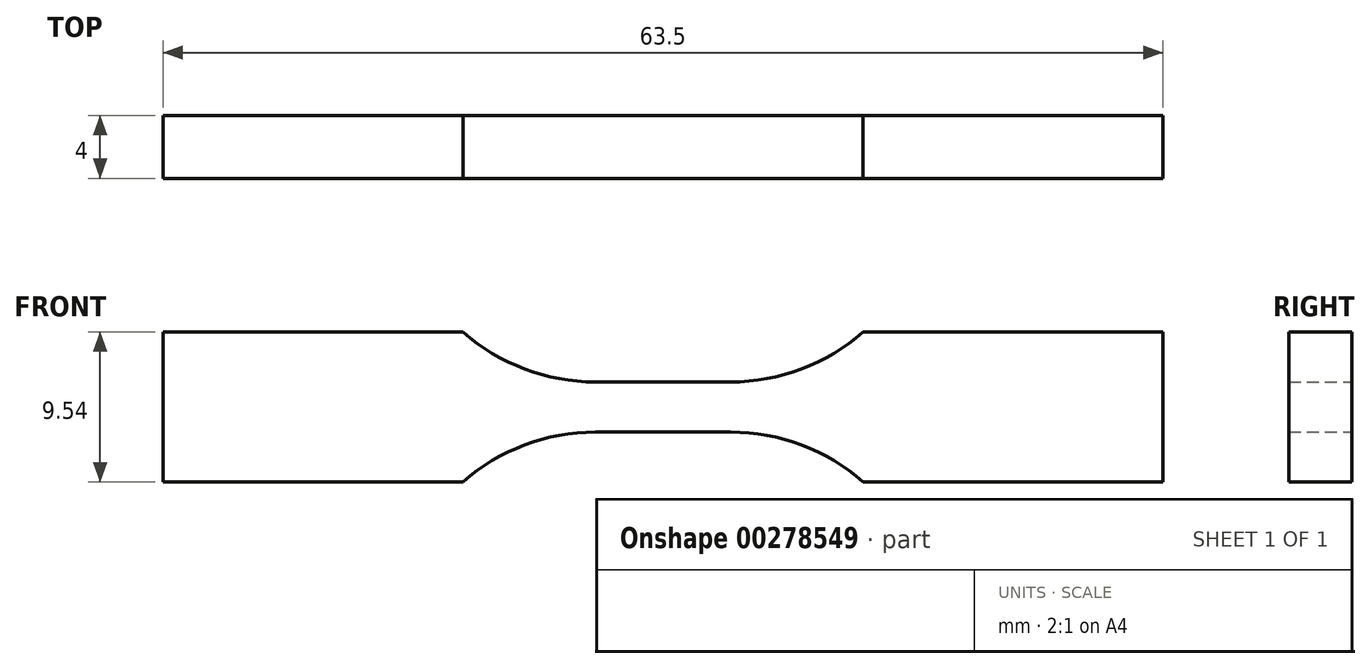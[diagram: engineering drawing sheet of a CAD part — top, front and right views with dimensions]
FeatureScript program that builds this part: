
annotation { "Feature Type Name" : "Feature", "Feature Type Description" : "" }
export const myFeature = defineFeature(function(context is Context, id is Id, definition is map)
    precondition{}
    {
        {
            var Q0;
            Q0=qCreatedBy(makeId("Front.planeOp"),FACE);
            var sketch = newSketch(context, id + "F0", { "sketchPlane" : qUnion([Q0])});
            skLineSegment(sketch, "E0", {"start": v(0, 1.6) * mm, "end": v(4.3, 1.6) * mm});
            skArc(sketch, "E1", {"start": v(4.3, 1.6) * mm, "mid": v(8.79, 2.41) * mm, "end": v(12.7, 4.77) * mm});
            skLineSegment(sketch, "E2", {"start": v(12.7, 4.77) * mm, "end": v(31.75, 4.77) * mm});
            skLineSegment(sketch, "E3.MirrorCS", {"start": v(12.7, -4.77) * mm, "end": v(31.75, -4.77) * mm});
            skLineSegment(sketch, "E4.MirrorCS", {"start": v(0, -1.6) * mm, "end": v(4.3, -1.6) * mm});
            skArc(sketch, "E5.MirrorCS", {"start": v(4.3, -1.6) * mm, "mid": v(8.79, -2.41) * mm, "end": v(12.7, -4.77) * mm});
            skArc(sketch, "E6.MirrorCS", {"start": v(-4.3, -1.6) * mm, "mid": v(-8.79, -2.41) * mm, "end": v(-12.7, -4.77) * mm});
            skLineSegment(sketch, "E7.MirrorCS", {"start": v(0, 1.6) * mm, "end": v(-4.3, 1.6) * mm});
            skArc(sketch, "E8.MirrorCS", {"start": v(-4.3, 1.6) * mm, "mid": v(-8.79, 2.41) * mm, "end": v(-12.7, 4.77) * mm});
            skLineSegment(sketch, "E9.MirrorCS", {"start": v(-12.7, -4.77) * mm, "end": v(-31.75, -4.77) * mm});
            skLineSegment(sketch, "E10.MirrorCS", {"start": v(0, -1.6) * mm, "end": v(-4.3, -1.6) * mm});
            skLineSegment(sketch, "E11.MirrorCS", {"start": v(-12.7, 4.77) * mm, "end": v(-31.75, 4.77) * mm});
            skLineSegment(sketch, "E12", {"start": v(-31.75, 4.77) * mm, "end": v(-31.75, -4.77) * mm});
            skLineSegment(sketch, "E13", {"start": v(31.75, 4.77) * mm, "end": v(31.75, -4.77) * mm});
            skSolve(sketch);
        }
        {
            var Q0;
            Q0=makeQuery(id+"F0.imprint","IMPRINT",FACE,{"disambiguationData":[TD([[makeQuery(id+"F0.imprint","IMPRINT",EDGE,{"derivedFrom":sQuery(id+"F0.wireOp",EDGE,"E0")}),-1.0]])]});
            extrude(context, id + "F1", {"entities" : qUnion([Q0]), "endBound" : BoundingType.SYMMETRIC, "depth" : 4 * mm});
        }
    });
